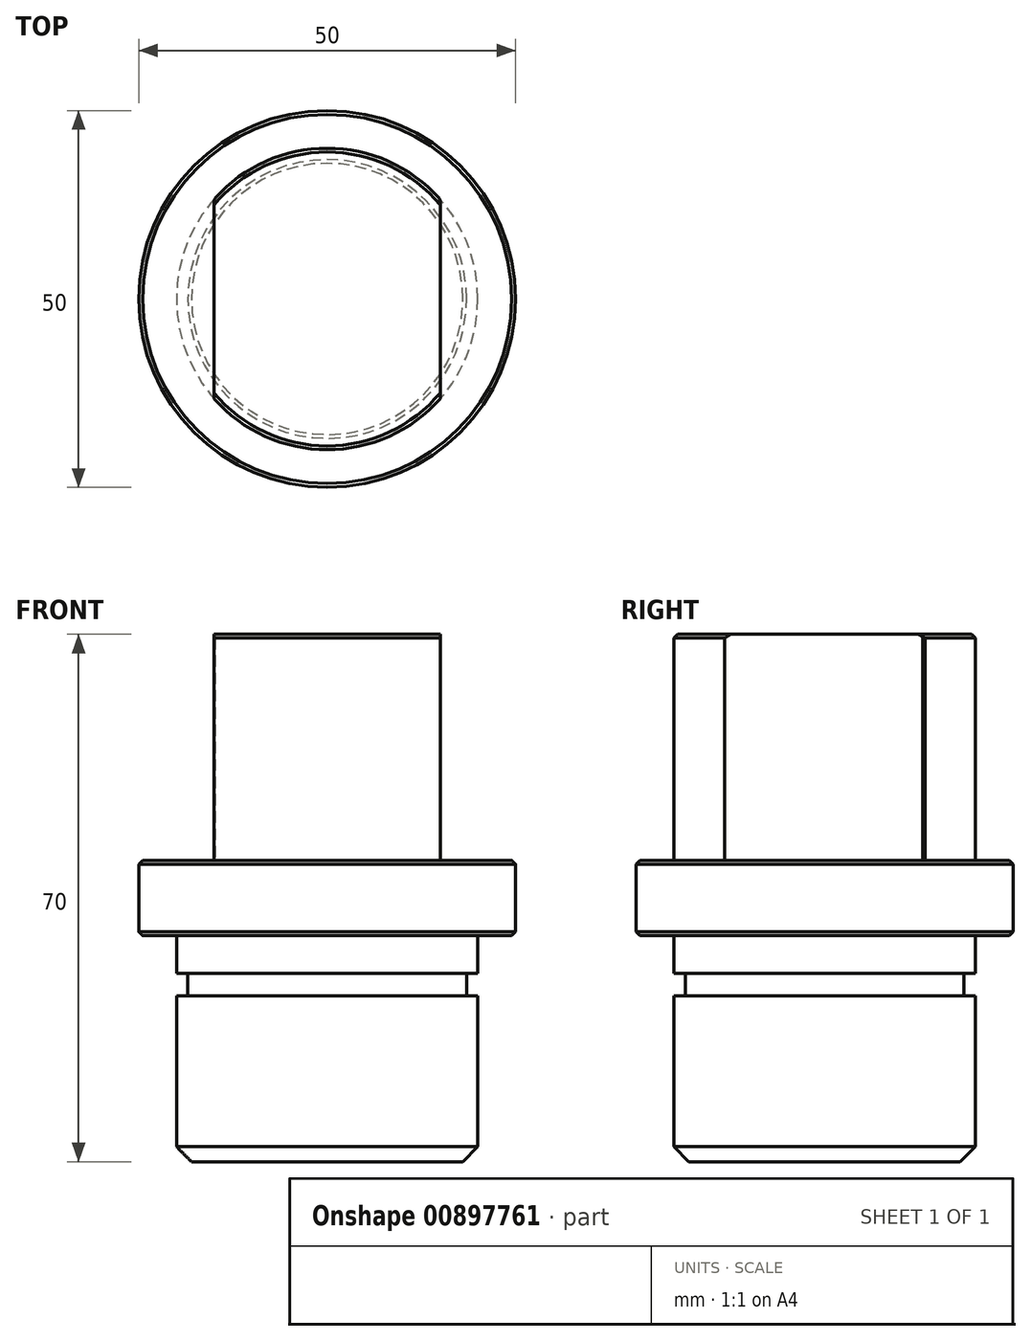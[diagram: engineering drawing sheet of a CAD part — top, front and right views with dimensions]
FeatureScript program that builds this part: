
annotation { "Feature Type Name" : "Feature", "Feature Type Description" : "" }
export const myFeature = defineFeature(function(context is Context, id is Id, definition is map)
    precondition{}
    {
        {
            var Q0;
            Q0=qCreatedBy(makeId("Front.planeOp"),FACE);
            var sketch = newSketch(context, id + "F0", { "sketchPlane" : qUnion([Q0])});
            skLineSegment(sketch, "E0", {"start": v(0, 0) * mm, "end": v(0, 90.6) * mm, "construction": true});
            skLineSegment(sketch, "E1", {"start": v(0, 0) * mm, "end": v(-20, 0) * mm});
            skLineSegment(sketch, "E2", {"start": v(-20, 0) * mm, "end": v(-20, 22) * mm});
            skLineSegment(sketch, "E3", {"start": v(-20, 22) * mm, "end": v(-18.5, 22) * mm});
            skLineSegment(sketch, "E4", {"start": v(-18.5, 22) * mm, "end": v(-18.5, 25) * mm});
            skLineSegment(sketch, "E5", {"start": v(-18.5, 25) * mm, "end": v(-20, 25) * mm});
            skLineSegment(sketch, "E6", {"start": v(-20, 25) * mm, "end": v(-20, 30) * mm});
            skLineSegment(sketch, "E7", {"start": v(-20, 30) * mm, "end": v(-25, 30) * mm});
            skLineSegment(sketch, "E8", {"start": v(-25, 30) * mm, "end": v(-25, 40) * mm});
            skLineSegment(sketch, "E9", {"start": v(-25, 40) * mm, "end": v(0, 40) * mm});
            skLineSegment(sketch, "E10", {"start": v(0, 40) * mm, "end": v(0, 0) * mm});
            skLineSegment(sketch, "E11", {"start": v(-20, 40) * mm, "end": v(-20, 70) * mm});
            skLineSegment(sketch, "E12", {"start": v(-20, 70) * mm, "end": v(0, 70) * mm});
            skLineSegment(sketch, "E13", {"start": v(0, 70) * mm, "end": v(0, 40) * mm});
            skSolve(sketch);
        }
        {
            var Q0;
            Q0 = qSketchRegion(id + "F0", true);
            var Q1;
            Q1=sQuery(id+"F0.wireOp",EDGE,"E0");
            revolve(context, id + "F1", {"surfaceOperationType" : NewSurfaceOperationType.NEW, "entities" : qUnion([Q0]), "axis" : qUnion([Q1]), "revolveType" : RevolveType.FULL});
        }
        {
            var Q0;
            Q0=makeQuery(id+"F1.opRevolve","SWEPT_EDGE",EDGE,{"disambiguationData":[OSD([sQuery(id+"F0.wireOp",EDGE,"E1"),sQuery(id+"F0.wireOp",EDGE,"E2")])]});
            chamfer(context, id + "F2", {"entities" : qUnion([Q0]), "width" : 2 * mm, "tangentPropagation" : true});
        }
        {
            var Q0;
            Q0=makeQuery(id+"F93mhjGZBbo61vx_1.boolean.opBoolean","SPLIT",EDGE,{"disambiguationData":[OD(1.0)],"derivedFrom":makeQuery(id+"F1.opRevolve","SWEPT_EDGE",EDGE,{"disambiguationData":[OSD([sQuery(id+"F0.wireOp",EDGE,"E8"),sQuery(id+"F0.wireOp",EDGE,"E9")])]})});
            var Q1;
            Q1=makeQuery(id+"F93mhjGZBbo61vx_1.boolean.opBoolean","COPY",EDGE,{"derivedFrom":makeQuery(id+"F93mhjGZBbo61vx_1.opExtrude","CAP_EDGE",EDGE,{"disambiguationData":[OSD([sQuery(id+"FLQaknwdEHvOekf_1.wireOp",EDGE,"VQ8pK9tN-pFNZ-yW9Q-pF08-JJ5UvjUHxZaM")])],"isStart":true})});
            var Q2;
            Q2=makeQuery(id+"F93mhjGZBbo61vx_1.boolean.opBoolean","SPLIT",EDGE,{"disambiguationData":[OD(0.0)],"derivedFrom":makeQuery(id+"F1.opRevolve","SWEPT_EDGE",EDGE,{"disambiguationData":[OSD([sQuery(id+"F0.wireOp",EDGE,"E8"),sQuery(id+"F0.wireOp",EDGE,"E9")])]})});
            var Q3;
            Q3=makeQuery(id+"F93mhjGZBbo61vx_1.boolean.opBoolean","COPY",EDGE,{"derivedFrom":makeQuery(id+"F93mhjGZBbo61vx_1.opExtrude","CAP_EDGE",EDGE,{"disambiguationData":[OSD([sQuery(id+"FLQaknwdEHvOekf_1.wireOp",EDGE,"2fb31226-47d0-4019-825d-e474a857e0290.MirrorCS")])],"isStart":true})});
            var Q4;
            Q4=makeQuery(id+"F93mhjGZBbo61vx_1.boolean.opBoolean","SPLIT",EDGE,{"disambiguationData":[OD(1.0)],"derivedFrom":makeQuery(id+"F1.opRevolve","SWEPT_EDGE",EDGE,{"disambiguationData":[OSD([sQuery(id+"F0.wireOp",EDGE,"E7"),sQuery(id+"F0.wireOp",EDGE,"E8")])]})});
            var Q5;
            Q5=makeQuery(id+"F93mhjGZBbo61vx_1.boolean.opBoolean","INTERSECT",EDGE,{"derivedFrom":[makeQuery(id+"F1.opRevolve","SWEPT_FACE",FACE,{"disambiguationData":[OSD([sQuery(id+"F0.wireOp",EDGE,"E7")])]}),makeQuery(id+"F93mhjGZBbo61vx_1.opExtrude","SWEPT_FACE",FACE,{"disambiguationData":[OSD([sQuery(id+"FLQaknwdEHvOekf_1.wireOp",EDGE,"VQ8pK9tN-pFNZ-yW9Q-pF08-JJ5UvjUHxZaM")])]})]});
            var Q6;
            Q6=makeQuery(id+"F93mhjGZBbo61vx_1.boolean.opBoolean","SPLIT",EDGE,{"disambiguationData":[OD(0.0)],"derivedFrom":makeQuery(id+"F1.opRevolve","SWEPT_EDGE",EDGE,{"disambiguationData":[OSD([sQuery(id+"F0.wireOp",EDGE,"E7"),sQuery(id+"F0.wireOp",EDGE,"E8")])]})});
            var Q7;
            Q7=makeQuery(id+"F93mhjGZBbo61vx_1.boolean.opBoolean","INTERSECT",EDGE,{"derivedFrom":[makeQuery(id+"F1.opRevolve","SWEPT_FACE",FACE,{"disambiguationData":[OSD([sQuery(id+"F0.wireOp",EDGE,"E7")])]}),makeQuery(id+"F93mhjGZBbo61vx_1.opExtrude","SWEPT_FACE",FACE,{"disambiguationData":[OSD([sQuery(id+"FLQaknwdEHvOekf_1.wireOp",EDGE,"2fb31226-47d0-4019-825d-e474a857e0290.MirrorCS")])]})]});
            chamfer(context, id + "F3", {"entities" : qUnion([Q0, Q1, Q2, Q3, Q4, Q5, Q6, Q7]), "width" : .5 * mm, "tangentPropagation" : true});
        }
        {
            var Q0;
            Q0=makeQuery(id+"F1.opRevolve","SWEPT_FACE",FACE,{"disambiguationData":[OSD([sQuery(id+"F0.wireOp",EDGE,"E12")])]});
            var sketch = newSketch(context, id + "F4", { "sketchPlane" : qUnion([Q0])});
            skCircle(sketch, "E14.0", {"center": v(0, 0) * mm, "radius": 20 * mm});
            skLineSegment(sketch, "E15", {"start": v(0, 0) * mm, "end": v(0, 38.28) * mm, "construction": true});
            skLineSegment(sketch, "E16", {"start": v(-15, 13.23) * mm, "end": v(-15, -13.23) * mm});
            skLineSegment(sketch, "E17.MirrorCS", {"start": v(15, 13.23) * mm, "end": v(15, -13.23) * mm});
            skSolve(sketch);
        }
        {
            var Q0;
            {var subQ0=sQuery(id+"F4.wireOp",EDGE,"E16");Q0=makeQuery(id+"F4.imprint","IMPRINT",FACE,{"disambiguationData":[TD([[makeQuery(id+"F4.imprint","IMPRINT",EDGE,{"derivedFrom":subQ0}),-1.0]])]});}
            var Q1;
            {var subQ0=sQuery(id+"F4.wireOp",EDGE,"E17.MirrorCS");Q1=makeQuery(id+"F4.imprint","IMPRINT",FACE,{"disambiguationData":[TD([[makeQuery(id+"F4.imprint","IMPRINT",EDGE,{"derivedFrom":subQ0}),1.0]])]});}
            var Q2;
            Q2=makeQuery(id+"F1.opRevolve","SWEPT_FACE",FACE,{"disambiguationData":[OSD([sQuery(id+"F0.wireOp",EDGE,"E9")])]});
            extrude(context, id + "F5", {"entities" : qUnion([Q0, Q1]), "operationType" : NewBodyOperationType.REMOVE, "endBound" : BoundingType.UP_TO_SURFACE, "oppositeDirection" : true, "depth" : 25 * mm, "endBoundEntityFace" : qUnion([Q2]), "offsetDistance" : 25 * mm});
        }
        {
            var Q0;
            Q0=makeQuery(id+"F5.boolean.opBoolean","COPY",EDGE,{"derivedFrom":makeQuery(id+"F5.opExtrude","CAP_EDGE",EDGE,{"disambiguationData":[OSD([sQuery(id+"F4.wireOp",EDGE,"E16")])],"isStart":true})});
            var Q1;
            {var subQ0=sQuery(id+"F4.wireOp",EDGE,"E16");var subQ1=sQuery(id+"F4.wireOp",EDGE,"E14.0");Q1=makeQuery(id+"F5.boolean.opBoolean","COPY",EDGE,{"derivedFrom":makeQuery(id+"F5.opExtrude","SWEPT_EDGE",EDGE,{"disambiguationData":[OSD([subQ1,subQ0]),TDD([makeQuery(id+"F4.imprint","INTERSECT",VERTEX,{"disambiguationData":[OD(1.0)],"derivedFrom":[subQ1,subQ0]})])]})});}
            var Q2;
            {var subQ0=sQuery(id+"F4.wireOp",EDGE,"E16");var subQ1=sQuery(id+"F4.wireOp",EDGE,"E14.0");Q2=makeQuery(id+"F5.boolean.opBoolean","COPY",EDGE,{"derivedFrom":makeQuery(id+"F5.opExtrude","SWEPT_EDGE",EDGE,{"disambiguationData":[OSD([subQ1,subQ0]),TDD([makeQuery(id+"F4.imprint","INTERSECT",VERTEX,{"disambiguationData":[OD(0.0)],"derivedFrom":[subQ1,subQ0]})])]})});}
            var Q3;
            {var subQ0=sQuery(id+"F4.wireOp",EDGE,"E17.MirrorCS");var subQ1=sQuery(id+"F4.wireOp",EDGE,"E14.0");Q3=makeQuery(id+"F5.boolean.opBoolean","COPY",EDGE,{"derivedFrom":makeQuery(id+"F5.opExtrude","SWEPT_EDGE",EDGE,{"disambiguationData":[OSD([subQ1,subQ0]),TDD([makeQuery(id+"F4.imprint","INTERSECT",VERTEX,{"disambiguationData":[OD(1.0)],"derivedFrom":[subQ1,subQ0]})])]})});}
            var Q4;
            {var subQ0=sQuery(id+"F4.wireOp",EDGE,"E17.MirrorCS");var subQ1=sQuery(id+"F4.wireOp",EDGE,"E14.0");Q4=makeQuery(id+"F5.boolean.opBoolean","COPY",EDGE,{"derivedFrom":makeQuery(id+"F5.opExtrude","SWEPT_EDGE",EDGE,{"disambiguationData":[OSD([subQ1,subQ0]),TDD([makeQuery(id+"F4.imprint","INTERSECT",VERTEX,{"disambiguationData":[OD(0.0)],"derivedFrom":[subQ1,subQ0]})])]})});}
            var Q5;
            Q5=makeQuery(id+"F5.boolean.opBoolean","COPY",EDGE,{"derivedFrom":makeQuery(id+"F5.opExtrude","CAP_EDGE",EDGE,{"disambiguationData":[OSD([sQuery(id+"F4.wireOp",EDGE,"E17.MirrorCS")])],"isStart":true})});
            var Q6;
            Q6=makeQuery(id+"F5.boolean.opBoolean","SPLIT",EDGE,{"disambiguationData":[OD(1.0)],"derivedFrom":makeQuery(id+"F1.opRevolve","SWEPT_EDGE",EDGE,{"disambiguationData":[OSD([sQuery(id+"F0.wireOp",EDGE,"E11"),sQuery(id+"F0.wireOp",EDGE,"E12")])]})});
            var Q7;
            Q7=makeQuery(id+"F5.boolean.opBoolean","SPLIT",EDGE,{"disambiguationData":[OD(0.0)],"derivedFrom":makeQuery(id+"F1.opRevolve","SWEPT_EDGE",EDGE,{"disambiguationData":[OSD([sQuery(id+"F0.wireOp",EDGE,"E11"),sQuery(id+"F0.wireOp",EDGE,"E12")])]})});
            chamfer(context, id + "F6", {"entities" : qUnion([Q0, Q1, Q2, Q3, Q4, Q5, Q6, Q7]), "width" : .5 * mm, "tangentPropagation" : true});
        }
    });
